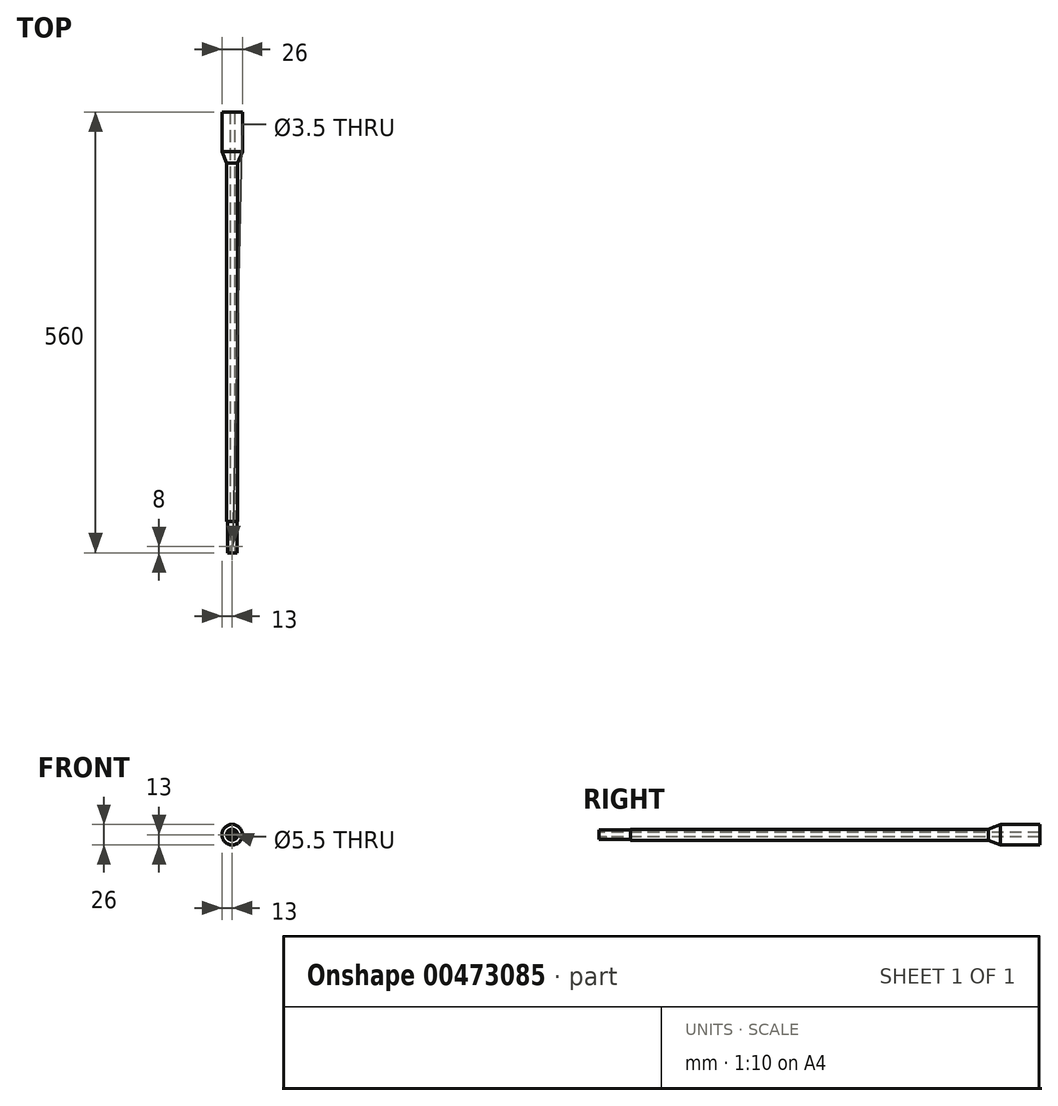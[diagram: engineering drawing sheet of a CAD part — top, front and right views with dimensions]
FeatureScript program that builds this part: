
annotation { "Feature Type Name" : "Feature", "Feature Type Description" : "" }
export const myFeature = defineFeature(function(context is Context, id is Id, definition is map)
    precondition{}
    {
        {
            var Q0;
            Q0=qCreatedBy(makeId("Front.planeOp"),FACE);
            var sketch = newSketch(context, id + "F0", { "sketchPlane" : qUnion([Q0])});
            skCircle(sketch, "E0", {"center": v(0, 0) * mm, "radius": 7 * mm});
            skSolve(sketch);
        }
        {
            var Q0;
            Q0=makeQuery(id+"F0.imprint","IMPRINT",FACE,{"disambiguationData":[TD([[makeQuery(id+"F0.imprint","IMPRINT",EDGE,{"derivedFrom":sQuery(id+"F0.wireOp",EDGE,"E0")}),1.0]])]});
            extrude(context, id + "F1", {"entities" : qUnion([Q0]), "oppositeDirection" : true, "depth" : 560 * mm});
        }
        {
            var Q0;
            Q0=makeQuery(id+"F1.opExtrude","CAP_FACE",FACE,{"disambiguationData":[OSD([sQuery(id+"F0.wireOp",EDGE,"E0")])],"isStart":true});
            var sketch = newSketch(context, id + "F2", { "sketchPlane" : qUnion([Q0])});
            skCircle(sketch, "E1", {"center": v(0, 0) * mm, "radius": 6 * mm});
            skSolve(sketch);
        }
        {
            var Q0;
            Q0=makeQuery(id+"F2.imprint","IMPRINT",FACE,{"disambiguationData":[TD([[makeQuery(id+"F2.imprint","IMPRINT",EDGE,{"derivedFrom":sQuery(id+"F2.wireOp",EDGE,"E1")}),-1.0]])]});
            extrude(context, id + "F3", {"entities" : qUnion([Q0]), "operationType" : NewBodyOperationType.REMOVE, "oppositeDirection" : true, "depth" : 40 * mm});
        }
        {
            var Q0;
            Q0=makeQuery(id+"F1.opExtrude","CAP_FACE",FACE,{"disambiguationData":[OSD([sQuery(id+"F0.wireOp",EDGE,"E0")])],"isStart":true});
            var sketch = newSketch(context, id + "F4", { "sketchPlane" : qUnion([Q0])});
            skCircle(sketch, "E2", {"center": v(0, 0) * mm, "radius": 2.75 * mm});
            skSolve(sketch);
        }
        {
            var Q0;
            Q0=makeQuery(id+"F4.imprint","IMPRINT",FACE,{"disambiguationData":[TD([[makeQuery(id+"F4.imprint","IMPRINT",EDGE,{"derivedFrom":sQuery(id+"F4.wireOp",EDGE,"E2")}),1.0]])]});
            extrude(context, id + "F5", {"entities" : qUnion([Q0]), "operationType" : NewBodyOperationType.REMOVE, "endBound" : BoundingType.THROUGH_ALL, "oppositeDirection" : true, "depth" : 25 * mm});
        }
        {
            var Q0;
            Q0=qCreatedBy(makeId("Top.planeOp"),FACE);
            var sketch = newSketch(context, id + "F6", { "sketchPlane" : qUnion([Q0])});
            skCircle(sketch, "E3", {"center": v(0, 8) * mm, "radius": 1.75 * mm});
            skSolve(sketch);
        }
        {
            var Q0;
            Q0=qSketchRegion(id+"F6",true);
            extrude(context, id + "F7", {"entities" : qUnion([Q0]), "operationType" : NewBodyOperationType.REMOVE, "oppositeDirection" : true, "depth" : 10 * mm});
        }
        {
            var Q0;
            Q0=makeQuery(id+"F1.opExtrude","CAP_FACE",FACE,{"disambiguationData":[OSD([sQuery(id+"F0.wireOp",EDGE,"E0")])],"isStart":false});
            var sketch = newSketch(context, id + "F8", { "sketchPlane" : qUnion([Q0])});
            skCircle(sketch, "E4", {"center": v(0, 0) * mm, "radius": 13 * mm});
            skSolve(sketch);
        }
        {
            var Q0;
            Q0=makeQuery(id+"F8.imprint","IMPRINT",FACE,{"disambiguationData":[TD([[makeQuery(id+"F8.imprint","IMPRINT",EDGE,{"derivedFrom":sQuery(id+"F8.wireOp",EDGE,"E4")}),1.0]])]});
            extrude(context, id + "F9", {"entities" : qUnion([Q0]), "operationType" : NewBodyOperationType.ADD, "oppositeDirection" : true, "depth" : 70 * mm});
        }
        {
            var Q0;
            Q0=makeQuery(id+"F9.opExtrude","CAP_EDGE",EDGE,{"disambiguationData":[OSD([sQuery(id+"F8.wireOp",EDGE,"E4")])],"isStart":false});
            chamfer(context, id + "F10", {"entities" : qUnion([Q0]), "chamferType" : ChamferType.TWO_OFFSETS, "width1" : 20 * mm, "oppositeDirection" : false, "width2" : 8 * mm, "tangentPropagation" : true});
        }
    });
